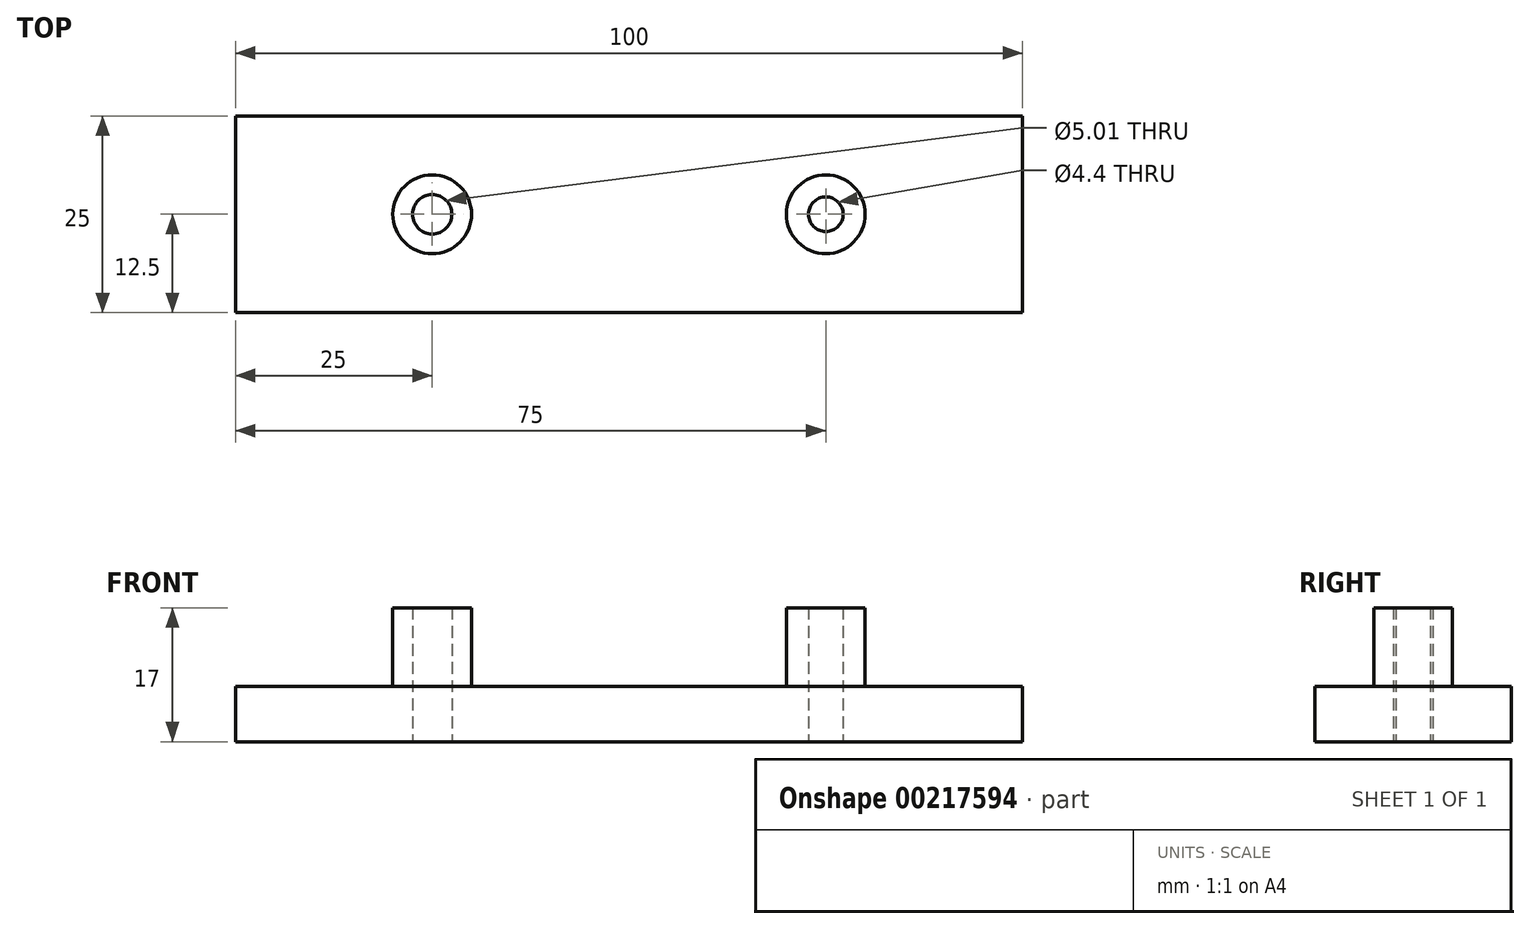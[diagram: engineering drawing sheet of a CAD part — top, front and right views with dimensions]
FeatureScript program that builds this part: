
annotation { "Feature Type Name" : "Feature", "Feature Type Description" : "" }
export const myFeature = defineFeature(function(context is Context, id is Id, definition is map)
    precondition{}
    {
        {
            var Q0;
            Q0=qCreatedBy(makeId("Top.planeOp"),FACE);
            var sketch = newSketch(context, id + "F0", { "sketchPlane" : qUnion([Q0])});
            skLineSegment(sketch, "E0", {"start": v(0, 39.27) * mm, "end": v(0, -28.86) * mm, "construction": true});
            skLineSegment(sketch, "E1", {"start": v(0, 0) * mm, "end": v(29.18, 0) * mm});
            skLineSegment(sketch, "E2.bottom", {"start": v(-50, 12.5) * mm, "end": v(50, 12.5) * mm});
            skLineSegment(sketch, "E2.top", {"start": v(-50, -12.5) * mm, "end": v(50, -12.5) * mm});
            skLineSegment(sketch, "E2.left", {"start": v(-50, 12.5) * mm, "end": v(-50, -12.5) * mm});
            skLineSegment(sketch, "E2.right", {"start": v(50, 12.5) * mm, "end": v(50, -12.5) * mm});
            skCircle(sketch, "E3", {"center": v(-25, 0) * mm, "radius": 2.5 * mm});
            skCircle(sketch, "E4", {"center": v(25, 0) * mm, "radius": 2.2 * mm});
            skSolve(sketch);
        }
        {
            var Q0;
            Q0=makeQuery(id+"F0.imprint","IMPRINT",FACE,{"disambiguationData":[TD([[makeQuery(id+"F0.imprint","IMPRINT",EDGE,{"derivedFrom":sQuery(id+"F0.wireOp",EDGE,"E2.bottom")}),-1.0]])]});
            extrude(context, id + "F1", {"entities" : qUnion([Q0]), "depth" : 7 * mm});
        }
        {
            var Q0;
            Q0=makeQuery(id+"F1.opExtrude","CAP_FACE",FACE,{"disambiguationData":[OSD([sQuery(id+"F0.wireOp",EDGE,"E2.bottom"),sQuery(id+"F0.wireOp",EDGE,"E2.top"),sQuery(id+"F0.wireOp",EDGE,"E2.left"),sQuery(id+"F0.wireOp",EDGE,"E2.right"),sQuery(id+"F0.wireOp",EDGE,"E3"),sQuery(id+"F0.wireOp",EDGE,"E4")])],"isStart":false});
            var sketch = newSketch(context, id + "F2", { "sketchPlane" : qUnion([Q0])});
            skCircle(sketch, "E5", {"center": v(-25, 0) * mm, "radius": 5 * mm});
            skCircle(sketch, "E6", {"center": v(25, 0) * mm, "radius": 5 * mm});
            skCircle(sketch, "E7.0", {"center": v(25, 0) * mm, "radius": 2.2 * mm});
            skCircle(sketch, "E8.0", {"center": v(-25, 0) * mm, "radius": 2.5 * mm});
            skSolve(sketch);
        }
        {
            var Q0;
            Q0 = qSketchRegion(id + "F2", true);
            extrude(context, id + "F3", {"entities" : qUnion([Q0]), "operationType" : NewBodyOperationType.ADD, "depth" : 10 * mm});
        }
    });
